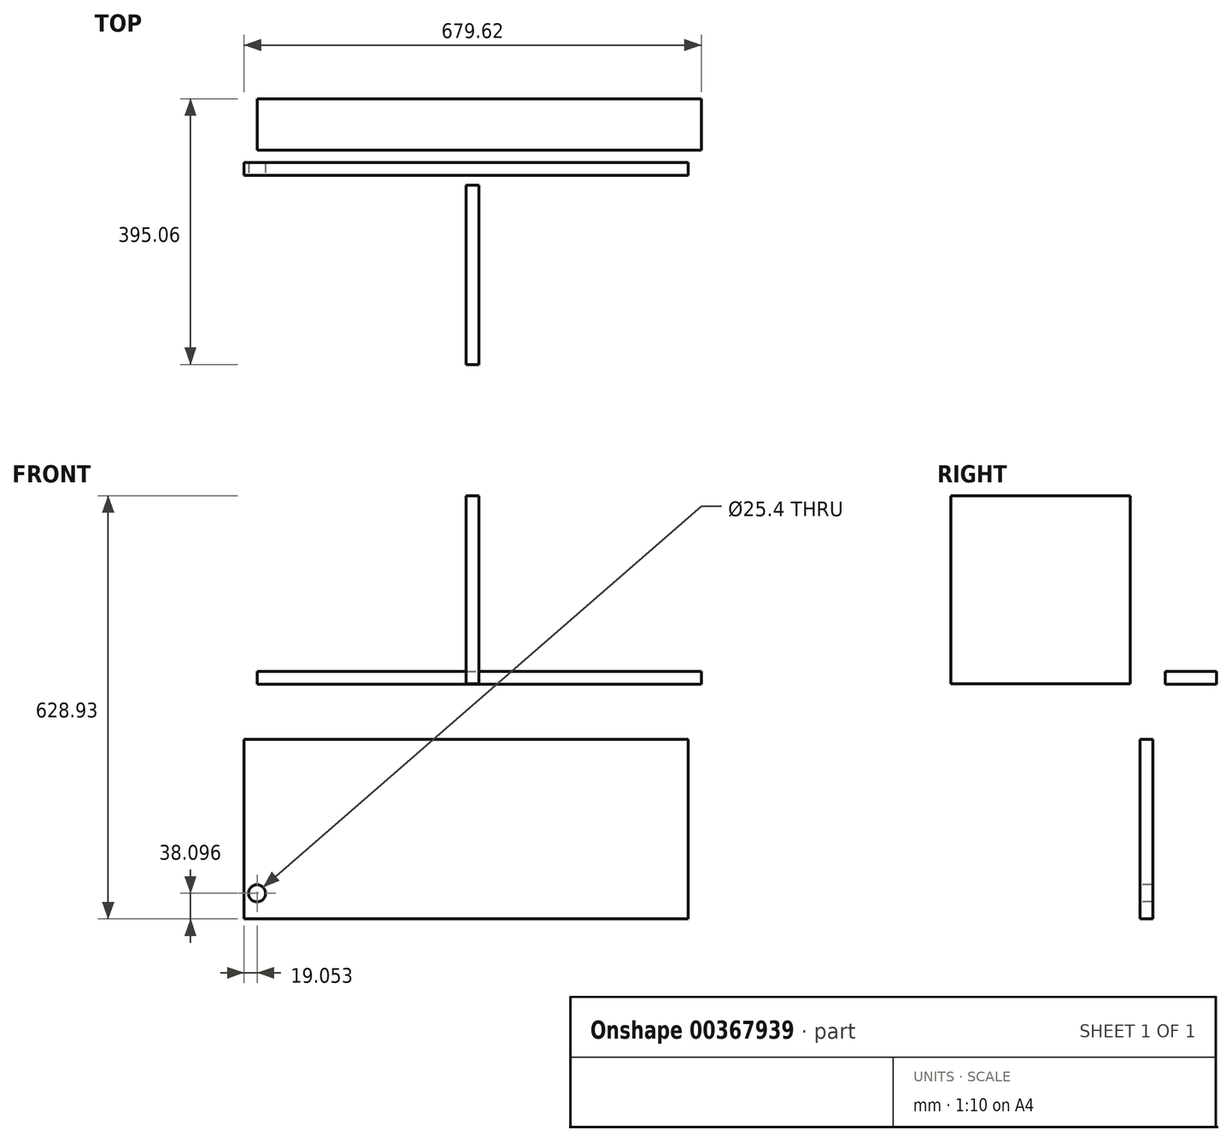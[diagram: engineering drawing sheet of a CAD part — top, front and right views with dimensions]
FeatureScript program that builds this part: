
annotation { "Feature Type Name" : "Feature", "Feature Type Description" : "" }
export const myFeature = defineFeature(function(context is Context, id is Id, definition is map)
    precondition{}
    {
        {
            var Q0;
            Q0=qCreatedBy(makeId("Front.planeOp"),FACE);
            var sketch = newSketch(context, id + "F0", { "sketchPlane" : qUnion([Q0])});
            skLineSegment(sketch, "E0.bottom", {"start": v(-329.8, -82.21) * mm, "end": v(330.6, -82.21) * mm});
            skLineSegment(sketch, "E0.top", {"start": v(-329.8, -348.91) * mm, "end": v(330.6, -348.91) * mm});
            skLineSegment(sketch, "E0.left", {"start": v(-329.8, -82.21) * mm, "end": v(-329.8, -348.91) * mm});
            skLineSegment(sketch, "E0.right", {"start": v(330.6, -82.21) * mm, "end": v(330.6, -348.91) * mm});
            skPoint(sketch, "E1", {"position": v(-310.76, -310.81) * mm});
            skSolve(sketch);
        }
        {
            var Q0;
            Q0 = qSketchRegion(id + "F0", true);
            extrude(context, id + "F1", {"entities" : qUnion([Q0]), "depth" : 19.05 * mm});
        }
        {
            var Q0;
            Q0=qCreatedBy(makeId("Top.planeOp"),FACE);
            var sketch = newSketch(context, id + "F2", { "sketchPlane" : qUnion([Q0])});
            skLineSegment(sketch, "E2.bottom", {"start": v(-310.6, 18.74) * mm, "end": v(349.8, 18.74) * mm});
            skLineSegment(sketch, "E2.top", {"start": v(-310.6, 94.94) * mm, "end": v(349.8, 94.94) * mm});
            skLineSegment(sketch, "E2.left", {"start": v(-310.6, 18.74) * mm, "end": v(-310.6, 94.94) * mm});
            skLineSegment(sketch, "E2.right", {"start": v(349.8, 18.74) * mm, "end": v(349.8, 94.94) * mm});
            skSolve(sketch);
        }
        {
            var Q0;
            Q0 = qSketchRegion(id + "F2", true);
            extrude(context, id + "F3", {"entities" : qUnion([Q0]), "depth" : 19.05 * mm});
        }
        {
            var Q0;
            Q0=qCreatedBy(makeId("Right.planeOp"),FACE);
            var sketch = newSketch(context, id + "F4", { "sketchPlane" : qUnion([Q0])});
            skLineSegment(sketch, "E3.bottom", {"start": v(-300.12, 280.02) * mm, "end": v(-33.42, 280.02) * mm});
            skLineSegment(sketch, "E3.top", {"start": v(-300.12, 0.62) * mm, "end": v(-33.42, 0.62) * mm});
            skLineSegment(sketch, "E3.left", {"start": v(-300.12, 280.02) * mm, "end": v(-300.12, 0.62) * mm});
            skLineSegment(sketch, "E3.right", {"start": v(-33.42, 280.02) * mm, "end": v(-33.42, 0.62) * mm});
            skSolve(sketch);
        }
        {
            var Q0;
            Q0 = qSketchRegion(id + "F4", true);
            extrude(context, id + "F5", {"entities" : qUnion([Q0]), "depth" : 19.05 * mm});
        }
        {
            var Q0;
            Q0=sQuery(id+"F0.wireOp",VERTEX,"E1");
            var Q1;
            Q1=makeQuery(id+"F1.opExtrude","SWEPT_BODY",BODY,{"disambiguationData":[OSD([sQuery(id+"F0.wireOp",EDGE,"E0.bottom"),sQuery(id+"F0.wireOp",EDGE,"E0.top"),sQuery(id+"F0.wireOp",EDGE,"E0.left"),sQuery(id+"F0.wireOp",EDGE,"E0.right")])]});
            hole(context, id + "F6", {"style" : HoleStyle.SIMPLE, "endStyle" : HoleEndStyle.THROUGH, "oppositeDirection" : true, "holeDiameter" : 25.4 * mm, "isTappedThrough" : true, "tappedDepth" : 12.7 * mm, "tapClearance" : 3, "locations" : qUnion([Q0]), "scope" : qUnion([Q1])});
        }
    });
